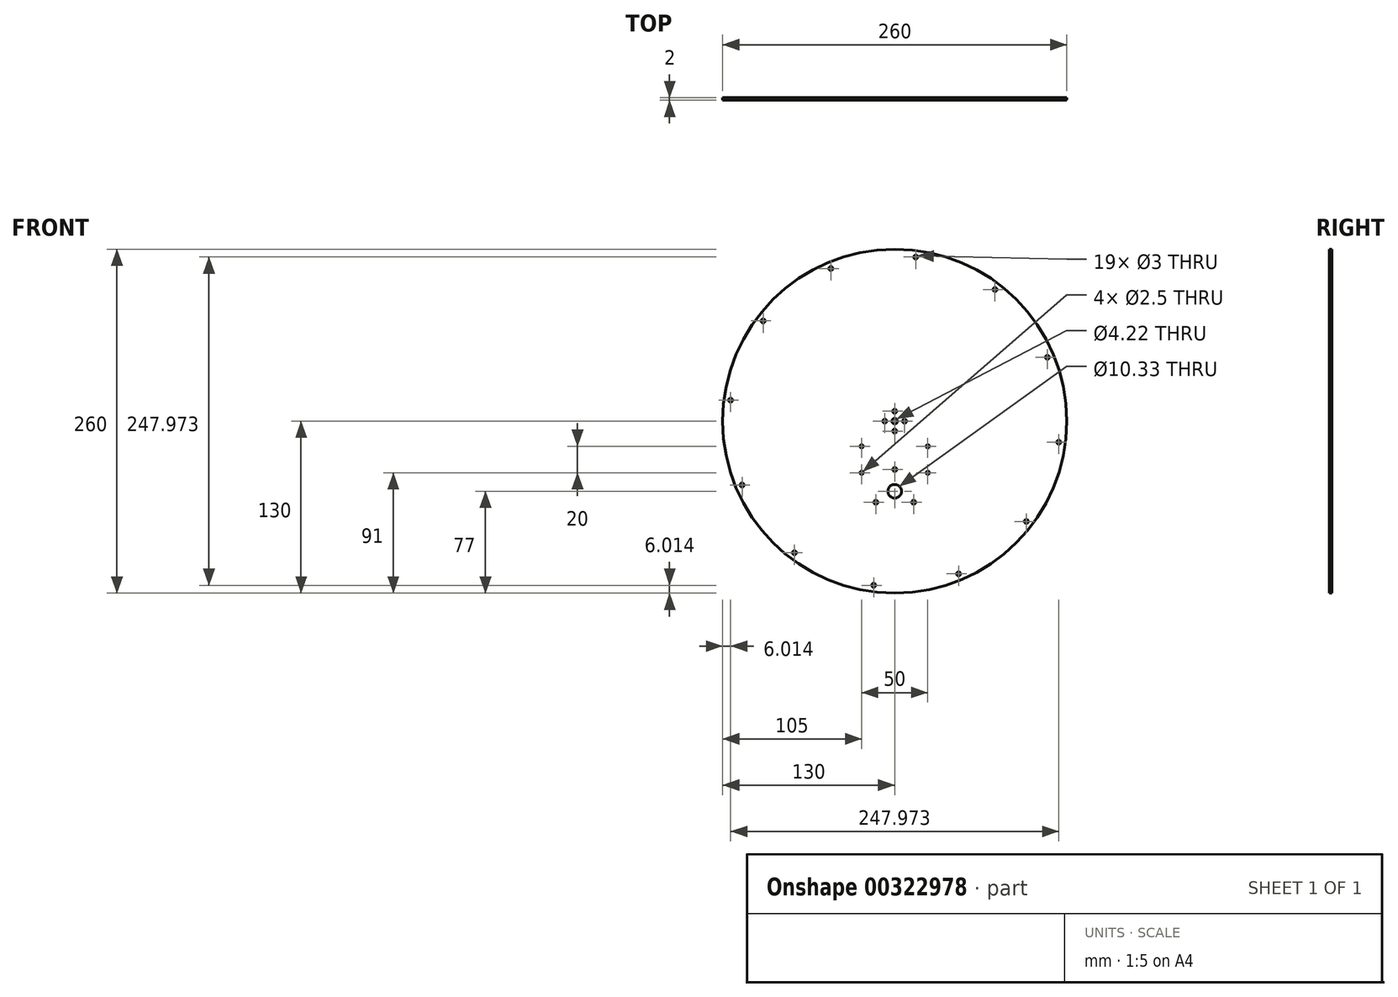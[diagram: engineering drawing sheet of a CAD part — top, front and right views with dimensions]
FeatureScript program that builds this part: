
annotation { "Feature Type Name" : "Feature", "Feature Type Description" : "" }
export const myFeature = defineFeature(function(context is Context, id is Id, definition is map)
    precondition{}
    {
        {
            var Q0;
            Q0=qCreatedBy(makeId("Front.planeOp"),FACE);
            var sketch = newSketch(context, id + "F0", { "sketchPlane" : qUnion([Q0])});
            skCircle(sketch, "E0", {"center": v(0, 0) * mm, "radius": 130 * mm});
            skCircle(sketch, "E1", {"center": v(0, 0) * mm, "radius": 5 * mm, "construction": true});
            skCircle(sketch, "E2", {"center": v(0, 0) * mm, "radius": 10 * mm, "construction": true});
            skLineSegment(sketch, "E3", {"start": v(0, 0) * mm, "end": v(130, 0) * mm, "construction": true});
            skLineSegment(sketch, "E4", {"start": v(0, 0) * mm, "end": v(0, 11.5) * mm, "construction": true});
            skLineSegment(sketch, "E5", {"start": v(0, 0) * mm, "end": v(0, -29) * mm, "construction": true});
            skLineSegment(sketch, "E6.bottom", {"start": v(25, -39) * mm, "end": v(-25, -39) * mm});
            skLineSegment(sketch, "E6.top", {"start": v(25, -19) * mm, "end": v(-25, -19) * mm});
            skLineSegment(sketch, "E6.left", {"start": v(25, -39) * mm, "end": v(25, -19) * mm});
            skLineSegment(sketch, "E6.right", {"start": v(-25, -39) * mm, "end": v(-25, -19) * mm});
            skPoint(sketch, "E6.middle", {"position": v(0, -29) * mm});
            skCircle(sketch, "E7", {"center": v(-25, -19) * mm, "radius": 1.25 * mm});
            skCircle(sketch, "E8", {"center": v(-25, -39) * mm, "radius": 1.25 * mm});
            skCircle(sketch, "E9.MirrorC", {"center": v(25, -19) * mm, "radius": 1.25 * mm});
            skCircle(sketch, "E10.MirrorC", {"center": v(25, -39) * mm, "radius": 1.25 * mm});
            skCircle(sketch, "E11", {"center": v(0, 0) * mm, "radius": 7.5 * mm, "construction": true});
            skCircle(sketch, "E12", {"center": v(0, -7.5) * mm, "radius": 1.5 * mm});
            skCircle(sketch, "E13", {"center": v(7.5, 0) * mm, "radius": 1.5 * mm});
            skCircle(sketch, "E14.MirrorC", {"center": v(0, 7.5) * mm, "radius": 1.5 * mm});
            skCircle(sketch, "E15.MirrorC", {"center": v(-7.5, 0) * mm, "radius": 1.5 * mm});
            skCircle(sketch, "E16", {"center": v(0, 0) * mm, "radius": 125 * mm, "construction": true});
            skLineSegment(sketch, "E17.0", {"start": v(-75.75, -99.43) * mm, "end": v(-115.32, -48.23) * mm, "construction": true});
            skLineSegment(sketch, "E17.1", {"start": v(-115.32, -48.23) * mm, "end": v(-123.99, 15.89) * mm, "construction": true});
            skLineSegment(sketch, "E17.2", {"start": v(-123.99, 15.89) * mm, "end": v(-99.43, 75.75) * mm, "construction": true});
            skLineSegment(sketch, "E17.3", {"start": v(-99.43, 75.75) * mm, "end": v(-48.23, 115.32) * mm, "construction": true});
            skLineSegment(sketch, "E17.4", {"start": v(-48.23, 115.32) * mm, "end": v(15.89, 123.99) * mm});
            skLineSegment(sketch, "E17.5", {"start": v(15.89, 123.99) * mm, "end": v(75.75, 99.43) * mm, "construction": true});
            skLineSegment(sketch, "E17.6", {"start": v(75.75, 99.43) * mm, "end": v(115.32, 48.23) * mm, "construction": true});
            skLineSegment(sketch, "E17.7", {"start": v(115.32, 48.23) * mm, "end": v(123.99, -15.89) * mm, "construction": true});
            skLineSegment(sketch, "E17.8", {"start": v(123.99, -15.89) * mm, "end": v(99.43, -75.75) * mm, "construction": true});
            skLineSegment(sketch, "E17.9", {"start": v(99.43, -75.75) * mm, "end": v(48.23, -115.32) * mm, "construction": true});
            skLineSegment(sketch, "E17.10", {"start": v(48.23, -115.32) * mm, "end": v(-15.89, -123.99) * mm, "construction": true});
            skLineSegment(sketch, "E17.11", {"start": v(-15.89, -123.99) * mm, "end": v(-75.75, -99.43) * mm, "construction": true});
            skCircle(sketch, "E18", {"center": v(123.99, -15.89) * mm, "radius": 1.5 * mm});
            skCircle(sketch, "E19", {"center": v(99.43, -75.75) * mm, "radius": 1.5 * mm});
            skCircle(sketch, "E20", {"center": v(48.23, -115.32) * mm, "radius": 1.5 * mm});
            skCircle(sketch, "E21", {"center": v(-15.89, -123.99) * mm, "radius": 1.5 * mm});
            skCircle(sketch, "E22", {"center": v(-75.75, -99.43) * mm, "radius": 1.5 * mm});
            skCircle(sketch, "E23", {"center": v(-115.32, -48.23) * mm, "radius": 1.5 * mm});
            skCircle(sketch, "E24", {"center": v(-123.99, 15.89) * mm, "radius": 1.5 * mm});
            skCircle(sketch, "E25", {"center": v(-99.43, 75.75) * mm, "radius": 1.5 * mm});
            skCircle(sketch, "E26", {"center": v(-48.23, 115.32) * mm, "radius": 5 * mm, "construction": true});
            skCircle(sketch, "E27", {"center": v(15.89, 123.99) * mm, "radius": 1.5 * mm});
            skCircle(sketch, "E28", {"center": v(75.75, 99.43) * mm, "radius": 1.5 * mm});
            skCircle(sketch, "E29", {"center": v(115.32, 48.23) * mm, "radius": 1.5 * mm});
            skCircle(sketch, "E30", {"center": v(-48.23, 115.32) * mm, "radius": 1.5 * mm});
            skCircle(sketch, "E31", {"center": v(0, 0) * mm, "radius": 2.11 * mm});
            skLineSegment(sketch, "E32", {"start": v(0, -29) * mm, "end": v(0, -53) * mm, "construction": true});
            skCircle(sketch, "E33", {"center": v(0, -53) * mm, "radius": 12 * mm, "construction": true});
            skCircle(sketch, "E34", {"center": v(0, -53) * mm, "radius": 17 * mm, "construction": true});
            skCircle(sketch, "E35", {"center": v(0, -53) * mm, "radius": 14.5 * mm, "construction": true});
            skCircle(sketch, "E36.cCircle", {"center": v(0, -53) * mm, "radius": 16.5 * mm, "construction": true});
            skCircle(sketch, "E37", {"center": v(0, -53) * mm, "radius": 5.16 * mm});
            skLineSegment(sketch, "E38.0", {"start": v(0, -36.5) * mm, "end": v(14.29, -61.25) * mm, "construction": true});
            skLineSegment(sketch, "E38.1", {"start": v(14.29, -61.25) * mm, "end": v(-14.29, -61.25) * mm, "construction": true});
            skLineSegment(sketch, "E38.2", {"start": v(-14.29, -61.25) * mm, "end": v(0, -36.5) * mm, "construction": true});
            skCircle(sketch, "E39", {"center": v(0, -36.5) * mm, "radius": 1.5 * mm});
            skCircle(sketch, "E40", {"center": v(-14.29, -61.25) * mm, "radius": 1.5 * mm});
            skCircle(sketch, "E41", {"center": v(14.29, -61.25) * mm, "radius": 1.5 * mm});
            skSolve(sketch);
        }
        {
            var Q0;
            Q0=makeQuery(id+"F0.imprint","IMPRINT",FACE,{"disambiguationData":[TD([[makeQuery(id+"F0.imprint","IMPRINT",EDGE,{"derivedFrom":sQuery(id+"F0.wireOp",EDGE,"E0")}),1.0]])]});
            var Q1;
            {var subQ5=sQuery(id+"F0.wireOp",EDGE,"E10.MirrorC");var subQ10=sQuery(id+"F0.wireOp",EDGE,"E6.bottom");var subQ11=makeQuery(id+"F0.imprint","INTERSECT",VERTEX,{"derivedFrom":[subQ10,subQ5]});Q1=makeQuery(id+"F0.imprint","IMPRINT",FACE,{"disambiguationData":[TD([[makeQuery(id+"F0.imprint","IMPRINT",EDGE,{"disambiguationData":[TD([[subQ11,-1.0]])],"derivedFrom":subQ10}),-1.0]])]});}
            extrude(context, id + "F1", {"entities" : qUnion([Q0, Q1]), "depth" : 2 * mm});
        }
    });
